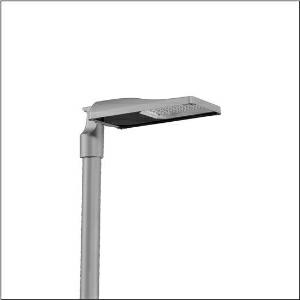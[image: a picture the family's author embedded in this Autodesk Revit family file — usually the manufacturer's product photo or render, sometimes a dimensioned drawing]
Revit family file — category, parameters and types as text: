
# Revit family: streetlight_sl_31_mini___st1_0a_5xh6d31b08ja_158d
name_source: partatom
category: Lighting Fixtures
units: mm (PartAtom-declared; Revit-internal decimal feet)

## family parameters
Cut with Voids When Loaded = No
Host = Face
Light Source = No
Part Type = Normal
Room Calculation Point = No
Round Connector Dimension = Use Diameter
Shared = No

## types (1)
- --- (1 x LED, 12140 lm, 81.1 W, 3000K)
    Apparent Load = 81 VA
    CIE Flux Codes = 40 73 97 100 100
    Color Rendering = 70
    Color Temperature = 3000K
    Default Elevation = 1800 mm
    Description = Streetlight SL 31 mini Easy, LST, Desk-Remote mast luminaire for post-top, side-entry; light control with lens of PMMA; light distribution: ST1.0a, direct asymmetric distribution, for standard-compliant lighting for roads and squares; LED: luminous flux: 12.140lm, light colour: 730, colour temperature: 3000K; luminous efficacy: 149,7lm/W; control: pre-setting: linear dimming characteristic, flexible luminous flux parameterisation, time-dependent luminous flux control, constant luminous flux control, power reduction, intelligent temperature release in ECG and LED module, overheat protection; luminaire housing, of diecast aluminium, Siteco® metallic grey (DB 702S), corrosivity category C5 high according to DIN EN ISO 12944; cover of toughened safety glass, transparent, opened without tools; mast flange of diecast aluminium, Siteco® metallic grey (DB 702S), spigot size: 76/60mm, mast flange included unmounted; with cable H07RN-F 3x 1.5mm², cable length: 10,5m, connection cable pre-assembled; mains connection: 220..240V, AC, 50/60Hz; power consumption (at start of service life): 81,1W / (at end of service life): 88,3W / (with reduced operation 50%): 36,4W; protection rating (complete): IP66; insulation class (complete): insulation class II (safety insulation); impact resistance: IK10; certification: CE, ENEC, ENEC+, VDE, UKCA; permissible operating ambient temperature for outdoor applications: -40..+50°C; packaging unit: 1 piece

Light Distribution: ST1.0a
    Height = 76 mm
    Lamp = 1 x LED
    Lamp Light Flux = 12140 lm
    Lamp Power = 81.1 W
    Lamp count = 1
    Length = 547 mm
    Luminous efficacy = 150 lm/W
    Manufacturer = Siteco
    ModVariant = No
    Model = 5XH6D31B08JA
    Number of Poles = 1
    OnlyDefault = Yes
    Power Factor = 1
    Product Name = Streetlight SL 31 mini | ST1.0a
    Product group = mast luminaire | pylon top
    ProductGroupID = 6100
    Protection Class = Protection class II
    Protection Degree = IP 66
    RLX_Detail_Level = 1
    RLX_Emergency_Light_Flux = 0 lm
    RLX_Emergency_Type = 0
    RLX_Emergency_Type_DB = No
    RlxData = <blob elided: 39757 chars, md5=192dfbe6>
    Socket = socket
    Standby Power = 0 W
    System Light Flux = 12140 lm
    System Power = 81 W
    Type Comments = factory setting: luminous flux: 100 % | dim-lin: 254 | 860 mA
    Type Image = l_1300326.jpg
    URL = http://relux.com
    VarID = @adj_070997
    Voltage = 0 V
    Weight = 0.00 kg
    Width = 265 mm

## geometry (parser evidence)
native form markers: Blend x4, Sweep x10
no freeform markers — native parametric forms only
